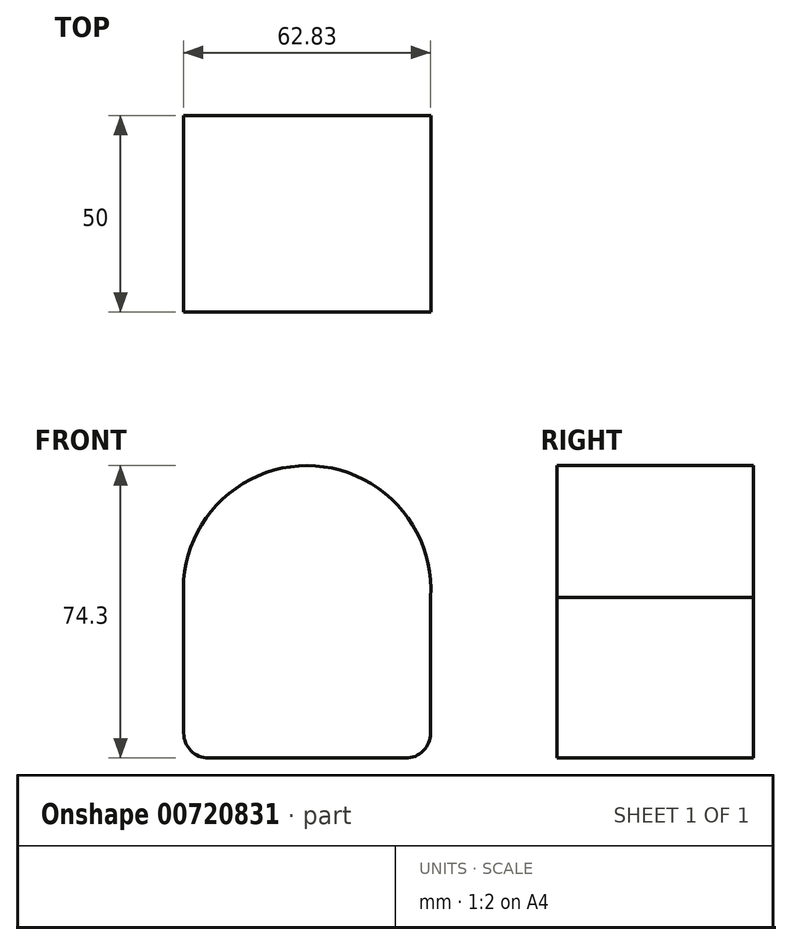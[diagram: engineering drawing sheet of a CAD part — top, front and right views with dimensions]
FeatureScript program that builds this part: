
annotation { "Feature Type Name" : "Feature", "Feature Type Description" : "" }
export const myFeature = defineFeature(function(context is Context, id is Id, definition is map)
    precondition{}
    {
        {
            var Q0;
            Q0=qCreatedBy(makeId("Front.planeOp"),FACE);
            var sketch = newSketch(context, id + "F0", { "sketchPlane" : qUnion([Q0])});
            skLineSegment(sketch, "E0.bottom", {"start": v(-28.2, 20.94) * mm, "end": v(34.5, 20.94) * mm});
            skLineSegment(sketch, "E0.top", {"start": v(-21.86, -19.95) * mm, "end": v(28.15, -19.95) * mm});
            skLineSegment(sketch, "E0.left", {"start": v(-28.2, 20.94) * mm, "end": v(-28.2, -13.6) * mm});
            skLineSegment(sketch, "E0.right", {"start": v(34.5, 20.94) * mm, "end": v(34.5, -13.6) * mm});
            skArc(sketch, "E1", {"start": v(34.5, 20.94) * mm, "mid": v(3.15, 54.35) * mm, "end": v(-28.2, 20.94) * mm});
            skPoint(sketch, "E2.visualSharp", {"position": v(-28.2, -19.95) * mm});
            skArc(sketch, "E2.filletArc", {"start": v(-28.2, -13.6) * mm, "mid": v(-26.35, -18.1) * mm, "end": v(-21.86, -19.95) * mm});
            skPoint(sketch, "E3.visualSharp", {"position": v(34.5, -19.95) * mm});
            skArc(sketch, "E3.filletArc", {"start": v(28.15, -19.95) * mm, "mid": v(32.64, -18.1) * mm, "end": v(34.5, -13.6) * mm});
            skPoint(sketch, "E4", {"position": v(-3.64, 11.3) * mm});
            skSolve(sketch);
        }
        {
            var Q0;
            Q0 = qSketchRegion(id + "F0", true);
            extrude(context, id + "F1", {"entities" : qUnion([Q0]), "depth" : 50 * mm, "offsetDistance" : 25.4 * mm});
        }
    });
